# Revit family: 1
name_source: partatom
category: Pipe Accessories
units: mm (PartAtom-declared; Revit-internal decimal feet)

## family parameters
Always vertical = No
Cut with Voids When Loaded = No
Part Type = Valve - Breaks Into
Round Connector Dimension = Use Diameter
Shared = No
Work Plane-Based = No

## types (40) — shared parameters
1 = 1 mm  [stored 0.00328084 ft]
10 = 10 mm  [stored 0.0328084 ft]
20 = 25 mm  [stored 0.082021 ft]
5 = 5 mm  [stored 0.0164042 ft]
50 = 80 mm
54-0700-33-0101100 = DN700_ PN10_ CTC
54-0700-33-0102100 = DN700_ PN10_ CTC
54-0700-33-1101100 = DN700_ PN16_ CTC
54-0700-33-1102100 = DN700_ PN16_ CTC
54-0700-33-1103100 = DN700_ PN16_ CTC
54-0700-34-0101100 = DN700_ PN10_ CTO
54-0700-34-0102100 = DN700_ PN10_ CTO
54-0700-34-1101100 = DN700_ PN16_ CTO
54-0700-34-1102100 = DN700_ PN16_ CTO
54-0700-34-1103100 = DN700_ PN16_ CTO
54-0800-33-0101100 = DN800_ PN10_ CTC
54-0800-33-0102100 = DN800_ PN10_ CTC
54-0800-33-0103100 = DN800_ PN10_ CTC
54-0800-33-1101100 = DN800_ PN16_ CTC
54-0800-33-1102100 = DN800_ PN16_ CTC
54-0800-33-1103100 = DN800_ PN16_ CTC
54-0800-33-1104100 = DN800_ PN16_ CTC
54-0800-34-0101100 = DN800_ PN10_ CTO
54-0800-34-0102100 = DN800_ PN10_ CTO
54-0800-34-1101100 = DN800_ PN16_ CTO
54-0800-34-1102100 = DN800_ PN16_ CTO
54-0900-33-0102100 = DN900_ PN10_ CTC
54-0900-33-1101100 = DN900_ PN16_ CTC
54-0900-33-1102100 = DN900_ PN16_ CTC
54-0900-33-1103100 = DN900_ PN16_ CTC
54-0900-33-1104100 = DN900_ PN16_ CTC
54-0900-34-0102100 = DN900_ PN10_ CTO
54-0900-34-0104100 = DN900_ PN10_ CTO
54-0900-34-1101100 = DN900_ PN16_ CTO
54-0900-34-1102100 = DN900_ PN16_ CTO
54-0900-34-1103100 = DN900_ PN16_ CTO
54-1000-33-0102100 = DN1000_ PN10_ CTC
54-1000-33-0103100 = DN1000_ PN10_ CTC
54-1000-33-0104100 = DN1000_ PN10_ CTC
54-1000-33-1102100 = DN1000_ PN16_ CTC
54-1000-33-1103100 = DN1000_ PN16_ CTC
54-1000-33-1104100 = DN1000_ PN16_ CTC
54-1000-34-0102100 = DN1000_ PN10_ CTO
54-1000-34-1102100 = DN1000_ PN16_ CTO
54-1000-34-1103100 = DN1000_ PN16_ CTO
BP_centre = 13 mm  [stored 0.0426509 ft]
Bypass_DN = 100 mm
Bypass_FL_OD = 140 mm
Bypass_L = 70 mm
Bypass_R = 26 mm
Bypass_R1 = 52 mm
Bypass_Vale_D1 = 112 mm
Bypass_Vale_D2 = 98 mm
Bypass_Vale_D3 = 112 mm
Bypass_Vale_D6 = 168 mm
Bypass_W = 65 mm
Description_ = AVK GATE VALVE, FLANGED, METAL SEATED, PN10/16
H = 782 mm
Raised_dis = 5 mm  [stored 0.0164042 ft]
Search_table = 54-3334-001 DN700-1000
Stem_H1 = 150 mm
Stem_H2 = 127.5 mm
Stem_H3 = 202.5 mm
URL product pages = https://www.avkvalves.com
zero-valued in all types: Bonnet_dim22, Default Elevation

## per-type parameters (varying)
- 54-0700-33-0101100: ACtuator_T=23.4 mm  [stored 0.0767717 ft]; ADN=700 mm; Actuator_FLR=87.5 mm; Actuator_dim1=52.5 mm; Actuator_dim2=31.5 mm  [stored 0.103346 ft]; Actuator_dim3=57.75 mm; Body_H=748.5 mm; Body_L=792.3 mm; Body_T=292.5 mm; Body_W=267.2 mm; Body_rib_T=13 mm  [stored 0.0426509 ft]; Bonnet_FL_L=834 mm; Bonnet_FL_T=61.75 mm; Bonnet_FL_W=334 mm; Bonnet_dim1=158.46 mm; Bonnet_dim2=93.52 mm; Bonnet_dim3=1287.42 mm; Bonnet_fillet=29.69 mm; Bore=350 mm; Bypass_D7=416.85 mm; Bypass_Location=172 mm; Bypass_Vale_D4=60.12 mm; Bypass_Vale_D5=84.17 mm; Bypass_Vale_T=48.1 mm; Bypass_sweep=416.85 mm; Cut_dis=30.88 mm; DN=700 mm; F=35 mm  [stored 0.114829 ft]; F1=15.75 mm  [stored 0.0516732 ft]; F2=116 mm; FL_T=32.5 mm  [stored 0.106627 ft]; Fillet=89.07 mm; H1=1497 mm; H2=450 mm; L=610 mm; OD=895 mm; OD1=900 mm; PN=10 mm  [stored 0.0328084 ft]; Raised_dia=794 mm; Rib_Actual=679.5 mm; Rib_H=598.8 mm; Rib_H1=300 mm; Rib_H2=450 mm; Rib_H3=550 mm; Rib_H4=650 mm; Rib_L=375.3 mm; Rib_W=150.3 mm; Stem_D1=17.5 mm  [stored 0.0574147 ft]; Stem_D2=26.25 mm  [stored 0.086122 ft]; Stem_dim=43.75 mm; W=1359 mm; W-W1=525 mm; W1=834 mm; W_half=525 mm; bottom_rib=447.5 mm; stem_dim=38.67 mm; stem_dim1=56.88 mm; sweep=4 mm  [stored 0.0131234 ft]; sweep_start=397 mm; wedge_dim1=293.92 mm
- 54-0700-33-0102100: ACtuator_T=23.4 mm  [stored 0.0767717 ft]; ADN=700 mm; Actuator_FLR=105 mm; Actuator_dim1=63 mm; Actuator_dim2=37.8 mm; Actuator_dim3=69.3 mm; Body_H=748.5 mm; Body_L=792.3 mm; Body_T=292.5 mm; Body_W=267.2 mm; Body_rib_T=13 mm  [stored 0.0426509 ft]; Bonnet_FL_L=834 mm; Bonnet_FL_T=61.75 mm; Bonnet_FL_W=334 mm; Bonnet_dim1=158.46 mm; Bonnet_dim2=93.52 mm; Bonnet_dim3=1287.42 mm; Bonnet_fillet=29.69 mm; Bore=350.05 mm; Bypass_D7=416.85 mm; Bypass_Location=172 mm; Bypass_Vale_D4=60.12 mm; Bypass_Vale_D5=84.17 mm; Bypass_Vale_T=48.1 mm; Bypass_sweep=416.85 mm; Cut_dis=30.88 mm; DN=700.1 mm; F=42 mm; F1=18.9 mm  [stored 0.0620079 ft]; F2=129 mm; FL_T=32.5 mm  [stored 0.106627 ft]; Fillet=89.07 mm; H1=1497 mm; H2=450 mm; L=610 mm; OD=895 mm; OD1=900 mm; PN=10 mm  [stored 0.0328084 ft]; Raised_dia=794 mm; Rib_Actual=679.5 mm; Rib_H=598.8 mm; Rib_H1=300 mm; Rib_H2=450 mm; Rib_H3=550 mm; Rib_H4=650 mm; Rib_L=375.3 mm; Rib_W=150.3 mm; Stem_D1=21 mm  [stored 0.0688976 ft]; Stem_D2=31.5 mm  [stored 0.103346 ft]; Stem_dim=52.5 mm; W=1359 mm; W-W1=525 mm; W1=834 mm; W_half=525 mm; bottom_rib=447.5 mm; stem_dim=43 mm; stem_dim1=68.25 mm; sweep=4 mm  [stored 0.0131234 ft]; sweep_start=397 mm; wedge_dim1=293.92 mm
- 54-0700-33-1101100: ACtuator_T=28.44 mm; ADN=700 mm; Actuator_FLR=87.5 mm; Actuator_dim1=52.5 mm; Actuator_dim2=31.5 mm  [stored 0.103346 ft]; Actuator_dim3=57.75 mm; Body_H=748.5 mm; Body_L=792.3 mm; Body_T=292.5 mm; Body_W=267.2 mm; Body_rib_T=15.8 mm  [stored 0.0518373 ft]; Bonnet_FL_L=834 mm; Bonnet_FL_T=75.05 mm; Bonnet_FL_W=334 mm; Bonnet_dim1=158.46 mm; Bonnet_dim2=93.52 mm; Bonnet_dim3=1287.42 mm; Bonnet_fillet=29.69 mm; Bore=350.06 mm; Bypass_D7=378 mm; Bypass_Location=172 mm; Bypass_Vale_D4=60.12 mm; Bypass_Vale_D5=84.17 mm; Bypass_Vale_T=48.1 mm; Bypass_sweep=378 mm; Cut_dis=37.53 mm; DN=700.11 mm; F=35 mm  [stored 0.114829 ft]; F1=15.75 mm  [stored 0.0516732 ft]; F2=116 mm; FL_T=39.5 mm; Fillet=89.07 mm; H1=1497 mm; H2=450 mm; L=610 mm; OD=880 mm; OD1=900 mm; PN=16 mm  [stored 0.0524934 ft]; Raised_dia=720 mm; Rib_Actual=679.5 mm; Rib_H=598.8 mm; Rib_H1=300 mm; Rib_H2=450 mm; Rib_H3=550 mm; Rib_H4=650 mm; Rib_L=375.3 mm; Rib_W=150.3 mm; Stem_D1=17.5 mm  [stored 0.0574147 ft]; Stem_D2=26.25 mm  [stored 0.086122 ft]; Stem_dim=43.75 mm; W=1359 mm; W-W1=525 mm; W1=834 mm; W_half=525 mm; bottom_rib=440 mm; stem_dim=38.67 mm; stem_dim1=56.88 mm; sweep=4 mm  [stored 0.0131234 ft]; sweep_start=360 mm; wedge_dim1=293.92 mm
- 54-0700-33-1102100: ACtuator_T=28.44 mm; ADN=700 mm; Actuator_FLR=105 mm; Actuator_dim1=63 mm; Actuator_dim2=37.8 mm; Actuator_dim3=69.3 mm; Body_H=748.5 mm; Body_L=792.3 mm; Body_T=292.5 mm; Body_W=267.2 mm; Body_rib_T=15.8 mm  [stored 0.0518373 ft]; Bonnet_FL_L=834 mm; Bonnet_FL_T=75.05 mm; Bonnet_FL_W=334 mm; Bonnet_dim1=158.46 mm; Bonnet_dim2=93.52 mm; Bonnet_dim3=1287.42 mm; Bonnet_fillet=29.69 mm; Bore=350.06 mm; Bypass_D7=378 mm; Bypass_Location=172 mm; Bypass_Vale_D4=60.12 mm; Bypass_Vale_D5=84.17 mm; Bypass_Vale_T=48.1 mm; Bypass_sweep=378 mm; Cut_dis=37.53 mm; DN=700.12 mm; F=42 mm; F1=18.9 mm  [stored 0.0620079 ft]; F2=129 mm; FL_T=39.5 mm; Fillet=89.07 mm; H1=1497 mm; H2=450 mm; L=610 mm; OD=880 mm; OD1=900 mm; PN=16 mm  [stored 0.0524934 ft]; Raised_dia=720 mm; Rib_Actual=679.5 mm; Rib_H=598.8 mm; Rib_H1=300 mm; Rib_H2=450 mm; Rib_H3=550 mm; Rib_H4=650 mm; Rib_L=375.3 mm; Rib_W=150.3 mm; Stem_D1=21 mm  [stored 0.0688976 ft]; Stem_D2=31.5 mm  [stored 0.103346 ft]; Stem_dim=52.5 mm; W=1359 mm; W-W1=525 mm; W1=834 mm; W_half=525 mm; bottom_rib=440 mm; stem_dim=43 mm; stem_dim1=68.25 mm; sweep=4 mm  [stored 0.0131234 ft]; sweep_start=360 mm; wedge_dim1=293.92 mm
- 54-0700-33-1103100: ACtuator_T=28.44 mm; ADN=700 mm; Actuator_FLR=150 mm; Actuator_dim1=90 mm; Actuator_dim2=54 mm; Actuator_dim3=99 mm; Body_H=748.5 mm; Body_L=997.5 mm; Body_T=342.5 mm; Body_W=291.2 mm; Body_rib_T=15.8 mm  [stored 0.0518373 ft]; Bonnet_FL_L=1050 mm; Bonnet_FL_T=75.05 mm; Bonnet_FL_W=364 mm; Bonnet_dim1=199.5 mm; Bonnet_dim2=101.92 mm; Bonnet_dim3=1287.42 mm; Bonnet_fillet=32.36 mm; Bore=350.07 mm; Bypass_D7=416.85 mm; Bypass_Location=172 mm; Bypass_Vale_D4=65.52 mm; Bypass_Vale_D5=91.73 mm; Bypass_Vale_T=52.42 mm; Bypass_sweep=416.85 mm; Cut_dis=37.53 mm; DN=700.13 mm; F=60 mm; F1=27 mm  [stored 0.0885827 ft]; F2=169 mm; FL_T=39.5 mm; Fillet=97.07 mm; H1=1497 mm; H2=450 mm; L=610 mm; OD=900 mm; OD1=900 mm; PN=16 mm  [stored 0.0524934 ft]; Raised_dia=794 mm; Rib_Actual=679.5 mm; Rib_H=598.8 mm; Rib_H1=300 mm; Rib_H2=450 mm; Rib_H3=550 mm; Rib_H4=650 mm; Rib_L=472.5 mm; Rib_W=163.8 mm; Stem_D1=30 mm  [stored 0.0984252 ft]; Stem_D2=45 mm; Stem_dim=75 mm; W=1359 mm; W-W1=525 mm; W1=834 mm; W_half=525 mm; bottom_rib=450 mm; stem_dim=56.33 mm; stem_dim1=97.5 mm; sweep=5 mm  [stored 0.0164042 ft]; sweep_start=397 mm; wedge_dim1=320.32 mm
- 54-0700-34-0101100: ACtuator_T=23.4 mm  [stored 0.0767717 ft]; ADN=700 mm; Actuator_FLR=87.5 mm; Actuator_dim1=52.5 mm; Actuator_dim2=31.5 mm  [stored 0.103346 ft]; Actuator_dim3=57.75 mm; Body_H=748.5 mm; Body_L=997.5 mm; Body_T=342.5 mm; Body_W=291.2 mm; Body_rib_T=13 mm  [stored 0.0426509 ft]; Bonnet_FL_L=1050 mm; Bonnet_FL_T=61.75 mm; Bonnet_FL_W=364 mm; Bonnet_dim1=199.5 mm; Bonnet_dim2=101.92 mm; Bonnet_dim3=1287.42 mm; Bonnet_fillet=32.36 mm; Bore=350.07 mm; Bypass_D7=416.85 mm; Bypass_Location=172 mm; Bypass_Vale_D4=65.52 mm; Bypass_Vale_D5=91.73 mm; Bypass_Vale_T=52.42 mm; Bypass_sweep=416.85 mm; Cut_dis=30.88 mm; DN=700.14 mm; F=35 mm  [stored 0.114829 ft]; F1=15.75 mm  [stored 0.0516732 ft]; F2=116 mm; FL_T=32.5 mm  [stored 0.106627 ft]; Fillet=97.07 mm; H1=1497 mm; H2=450 mm; L=610 mm; OD=895 mm; OD1=900 mm; PN=10 mm  [stored 0.0328084 ft]; Raised_dia=794 mm; Rib_Actual=679.5 mm; Rib_H=598.8 mm; Rib_H1=300 mm; Rib_H2=450 mm; Rib_H3=550 mm; Rib_H4=650 mm; Rib_L=472.5 mm; Rib_W=163.8 mm; Stem_D1=17.5 mm  [stored 0.0574147 ft]; Stem_D2=26.25 mm  [stored 0.086122 ft]; Stem_dim=43.75 mm; W=1359 mm; W-W1=525 mm; W1=834 mm; W_half=525 mm; bottom_rib=447.5 mm; stem_dim=38.67 mm; stem_dim1=56.88 mm; sweep=5 mm  [stored 0.0164042 ft]; sweep_start=397 mm; wedge_dim1=320.32 mm
- 54-0700-34-0102100: ACtuator_T=23.4 mm  [stored 0.0767717 ft]; ADN=700 mm; Actuator_FLR=105 mm; Actuator_dim1=63 mm; Actuator_dim2=37.8 mm; Actuator_dim3=69.3 mm; Body_H=748.5 mm; Body_L=997.5 mm; Body_T=342.5 mm; Body_W=291.2 mm; Body_rib_T=13 mm  [stored 0.0426509 ft]; Bonnet_FL_L=1050 mm; Bonnet_FL_T=61.75 mm; Bonnet_FL_W=364 mm; Bonnet_dim1=199.5 mm; Bonnet_dim2=101.92 mm; Bonnet_dim3=1287.42 mm; Bonnet_fillet=32.36 mm; Bore=350.08 mm; Bypass_D7=416.85 mm; Bypass_Location=172 mm; Bypass_Vale_D4=65.52 mm; Bypass_Vale_D5=91.73 mm; Bypass_Vale_T=52.42 mm; Bypass_sweep=416.85 mm; Cut_dis=30.88 mm; DN=700.15 mm; F=42 mm; F1=18.9 mm  [stored 0.0620079 ft]; F2=129 mm; FL_T=32.5 mm  [stored 0.106627 ft]; Fillet=97.07 mm; H1=1497 mm; H2=450 mm; L=610 mm; OD=895 mm; OD1=900 mm; PN=10 mm  [stored 0.0328084 ft]; Raised_dia=794 mm; Rib_Actual=679.5 mm; Rib_H=598.8 mm; Rib_H1=300 mm; Rib_H2=450 mm; Rib_H3=550 mm; Rib_H4=650 mm; Rib_L=472.5 mm; Rib_W=163.8 mm; Stem_D1=21 mm  [stored 0.0688976 ft]; Stem_D2=31.5 mm  [stored 0.103346 ft]; Stem_dim=52.5 mm; W=1359 mm; W-W1=525 mm; W1=834 mm; W_half=525 mm; bottom_rib=447.5 mm; stem_dim=43 mm; stem_dim1=68.25 mm; sweep=5 mm  [stored 0.0164042 ft]; sweep_start=397 mm; wedge_dim1=320.32 mm
- 54-0700-34-1101100: ACtuator_T=28.44 mm; ADN=700 mm; Actuator_FLR=87.5 mm; Actuator_dim1=52.5 mm; Actuator_dim2=31.5 mm  [stored 0.103346 ft]; Actuator_dim3=57.75 mm; Body_H=748.5 mm; Body_L=997.5 mm; Body_T=342.5 mm; Body_W=291.2 mm; Body_rib_T=15.8 mm  [stored 0.0518373 ft]; Bonnet_FL_L=1050 mm; Bonnet_FL_T=75.05 mm; Bonnet_FL_W=364 mm; Bonnet_dim1=199.5 mm; Bonnet_dim2=101.92 mm; Bonnet_dim3=1287.42 mm; Bonnet_fillet=32.36 mm; Bore=350.08 mm; Bypass_D7=416.85 mm; Bypass_Location=172 mm; Bypass_Vale_D4=65.52 mm; Bypass_Vale_D5=91.73 mm; Bypass_Vale_T=52.42 mm; Bypass_sweep=416.85 mm; Cut_dis=37.53 mm; DN=700.16 mm; F=35 mm  [stored 0.114829 ft]; F1=15.75 mm  [stored 0.0516732 ft]; F2=116 mm; FL_T=39.5 mm; Fillet=97.07 mm; H1=1497 mm; H2=450 mm; L=610 mm; OD=900 mm; OD1=900 mm; PN=16 mm  [stored 0.0524934 ft]; Raised_dia=794 mm; Rib_Actual=679.5 mm; Rib_H=598.8 mm; Rib_H1=300 mm; Rib_H2=450 mm; Rib_H3=550 mm; Rib_H4=650 mm; Rib_L=472.5 mm; Rib_W=163.8 mm; Stem_D1=17.5 mm  [stored 0.0574147 ft]; Stem_D2=26.25 mm  [stored 0.086122 ft]; Stem_dim=43.75 mm; W=1359 mm; W-W1=525 mm; W1=834 mm; W_half=525 mm; bottom_rib=450 mm; stem_dim=38.67 mm; stem_dim1=56.88 mm; sweep=5 mm  [stored 0.0164042 ft]; sweep_start=397 mm; wedge_dim1=320.32 mm
- 54-0700-34-1102100: ACtuator_T=28.44 mm; ADN=700 mm; Actuator_FLR=105 mm; Actuator_dim1=63 mm; Actuator_dim2=37.8 mm; Actuator_dim3=69.3 mm; Body_H=748.5 mm; Body_L=997.5 mm; Body_T=342.5 mm; Body_W=291.2 mm; Body_rib_T=15.8 mm  [stored 0.0518373 ft]; Bonnet_FL_L=1050 mm; Bonnet_FL_T=75.05 mm; Bonnet_FL_W=364 mm; Bonnet_dim1=199.5 mm; Bonnet_dim2=101.92 mm; Bonnet_dim3=1287.42 mm; Bonnet_fillet=32.36 mm; Bore=350.09 mm; Bypass_D7=416.85 mm; Bypass_Location=172 mm; Bypass_Vale_D4=65.52 mm; Bypass_Vale_D5=91.73 mm; Bypass_Vale_T=52.42 mm; Bypass_sweep=416.85 mm; Cut_dis=37.53 mm; DN=700.17 mm; F=42 mm; F1=18.9 mm  [stored 0.0620079 ft]; F2=129 mm; FL_T=39.5 mm; Fillet=97.07 mm; H1=1497 mm; H2=450 mm; L=610 mm; OD=900 mm; OD1=900 mm; PN=16 mm  [stored 0.0524934 ft]; Raised_dia=794 mm; Rib_Actual=679.5 mm; Rib_H=598.8 mm; Rib_H1=300 mm; Rib_H2=450 mm; Rib_H3=550 mm; Rib_H4=650 mm; Rib_L=472.5 mm; Rib_W=163.8 mm; Stem_D1=21 mm  [stored 0.0688976 ft]; Stem_D2=31.5 mm  [stored 0.103346 ft]; Stem_dim=52.5 mm; W=1359 mm; W-W1=525 mm; W1=834 mm; W_half=525 mm; bottom_rib=450 mm; stem_dim=43 mm; stem_dim1=68.25 mm; sweep=5 mm  [stored 0.0164042 ft]; sweep_start=397 mm; wedge_dim1=320.32 mm
- 54-0700-34-1103100: ACtuator_T=28.44 mm; ADN=700 mm; Actuator_FLR=150 mm; Actuator_dim1=90 mm; Actuator_dim2=54 mm; Actuator_dim3=99 mm; Body_H=748.5 mm; Body_L=997.5 mm; Body_T=342.5 mm; Body_W=291.2 mm; Body_rib_T=15.8 mm  [stored 0.0518373 ft]; Bonnet_FL_L=1050 mm; Bonnet_FL_T=75.05 mm; Bonnet_FL_W=364 mm; Bonnet_dim1=199.5 mm; Bonnet_dim2=101.92 mm; Bonnet_dim3=1287.42 mm; Bonnet_fillet=32.36 mm; Bore=350.09 mm; Bypass_D7=416.85 mm; Bypass_Location=172 mm; Bypass_Vale_D4=65.52 mm; Bypass_Vale_D5=91.73 mm; Bypass_Vale_T=52.42 mm; Bypass_sweep=416.85 mm; Cut_dis=37.53 mm; DN=700.18 mm; F=60 mm; F1=27 mm  [stored 0.0885827 ft]; F2=169 mm; FL_T=39.5 mm; Fillet=97.07 mm; H1=1497 mm; H2=450 mm; L=610 mm; OD=900 mm; OD1=900 mm; PN=16 mm  [stored 0.0524934 ft]; Raised_dia=794 mm; Rib_Actual=679.5 mm; Rib_H=598.8 mm; Rib_H1=300 mm; Rib_H2=450 mm; Rib_H3=550 mm; Rib_H4=650 mm; Rib_L=472.5 mm; Rib_W=163.8 mm; Stem_D1=30 mm  [stored 0.0984252 ft]; Stem_D2=45 mm; Stem_dim=75 mm; W=1359 mm; W-W1=525 mm; W1=834 mm; W_half=525 mm; bottom_rib=450 mm; stem_dim=56.33 mm; stem_dim1=97.5 mm; sweep=5 mm  [stored 0.0164042 ft]; sweep_start=397 mm; wedge_dim1=320.32 mm
- 54-0800-33-0101100: ACtuator_T=25.2 mm  [stored 0.0826772 ft]; ADN=800 mm; Actuator_FLR=87.5 mm; Actuator_dim1=52.5 mm; Actuator_dim2=31.5 mm  [stored 0.103346 ft]; Actuator_dim3=57.75 mm; Body_H=844.5 mm; Body_L=997.5 mm; Body_T=342.5 mm; Body_W=291.2 mm; Body_rib_T=14 mm  [stored 0.0459318 ft]; Bonnet_FL_L=1050 mm; Bonnet_FL_T=66.5 mm; Bonnet_FL_W=364 mm; Bonnet_dim1=199.5 mm; Bonnet_dim2=101.92 mm; Bonnet_dim3=1452.54 mm; Bonnet_fillet=32.36 mm; Bore=400 mm; Bypass_D7=473.03 mm; Bypass_Location=172 mm; Bypass_Vale_D4=65.52 mm; Bypass_Vale_D5=91.73 mm; Bypass_Vale_T=52.42 mm; Bypass_sweep=473.03 mm; Cut_dis=33.25 mm  [stored 0.109088 ft]; DN=800 mm; F=35 mm  [stored 0.114829 ft]; F1=15.75 mm  [stored 0.0516732 ft]; F2=116 mm; FL_T=35 mm  [stored 0.114829 ft]; Fillet=97.07 mm; H1=1689 mm; H2=535 mm; L=660 mm; OD=1015 mm; OD1=1070 mm; PN=10 mm  [stored 0.0328084 ft]; Raised_dia=901 mm; Rib_Actual=744 mm; Rib_H=675.6 mm; Rib_H1=190 mm; Rib_H2=550 mm; Rib_H3=650 mm; Rib_H4=750 mm; Rib_L=472.5 mm; Rib_W=163.8 mm; Stem_D1=17.5 mm  [stored 0.0574147 ft]; Stem_D2=26.25 mm  [stored 0.086122 ft]; Stem_dim=43.75 mm; W=1488 mm; W-W1=580 mm; W1=908 mm; W_half=580 mm; bottom_rib=507.5 mm; stem_dim=38.67 mm; stem_dim1=56.88 mm; sweep=5 mm  [stored 0.0164042 ft]; sweep_start=450.5 mm; wedge_dim1=320.32 mm
- 54-0800-33-0102100: ACtuator_T=25.2 mm  [stored 0.0826772 ft]; ADN=800 mm; Actuator_FLR=105 mm; Actuator_dim1=63 mm; Actuator_dim2=37.8 mm; Actuator_dim3=69.3 mm; Body_H=844.5 mm; Body_L=997.5 mm; Body_T=342.5 mm; Body_W=291.2 mm; Body_rib_T=14 mm  [stored 0.0459318 ft]; Bonnet_FL_L=1050 mm; Bonnet_FL_T=66.5 mm; Bonnet_FL_W=364 mm; Bonnet_dim1=199.5 mm; Bonnet_dim2=101.92 mm; Bonnet_dim3=1452.54 mm; Bonnet_fillet=32.36 mm; Bore=400.05 mm; Bypass_D7=473.03 mm; Bypass_Location=172 mm; Bypass_Vale_D4=65.52 mm; Bypass_Vale_D5=91.73 mm; Bypass_Vale_T=52.42 mm; Bypass_sweep=473.03 mm; Cut_dis=33.25 mm  [stored 0.109088 ft]; DN=800.1 mm; F=42 mm; F1=18.9 mm  [stored 0.0620079 ft]; F2=129 mm; FL_T=35 mm  [stored 0.114829 ft]; Fillet=97.07 mm; H1=1689 mm; H2=535 mm; L=660 mm; OD=1015 mm; OD1=1070 mm; PN=10 mm  [stored 0.0328084 ft]; Raised_dia=901 mm; Rib_Actual=744 mm; Rib_H=675.6 mm; Rib_H1=190 mm; Rib_H2=550 mm; Rib_H3=650 mm; Rib_H4=750 mm; Rib_L=472.5 mm; Rib_W=163.8 mm; Stem_D1=21 mm  [stored 0.0688976 ft]; Stem_D2=31.5 mm  [stored 0.103346 ft]; Stem_dim=52.5 mm; W=1488 mm; W-W1=580 mm; W1=908 mm; W_half=580 mm; bottom_rib=507.5 mm; stem_dim=43 mm; stem_dim1=68.25 mm; sweep=5 mm  [stored 0.0164042 ft]; sweep_start=450.5 mm; wedge_dim1=320.32 mm
- 54-0800-33-0103100: ACtuator_T=25.2 mm  [stored 0.0826772 ft]; ADN=800 mm; Actuator_FLR=150 mm; Actuator_dim1=90 mm; Actuator_dim2=54 mm; Actuator_dim3=99 mm; Body_H=844.5 mm; Body_L=997.5 mm; Body_T=342.5 mm; Body_W=291.2 mm; Body_rib_T=14 mm  [stored 0.0459318 ft]; Bonnet_FL_L=1050 mm; Bonnet_FL_T=66.5 mm; Bonnet_FL_W=364 mm; Bonnet_dim1=199.5 mm; Bonnet_dim2=101.92 mm; Bonnet_dim3=1452.54 mm; Bonnet_fillet=32.36 mm; Bore=400.06 mm; Bypass_D7=473.03 mm; Bypass_Location=172 mm; Bypass_Vale_D4=65.52 mm; Bypass_Vale_D5=91.73 mm; Bypass_Vale_T=52.42 mm; Bypass_sweep=473.03 mm; Cut_dis=33.25 mm  [stored 0.109088 ft]; DN=800.11 mm; F=60 mm; F1=27 mm  [stored 0.0885827 ft]; F2=169 mm; FL_T=35 mm  [stored 0.114829 ft]; Fillet=97.07 mm; H1=1689 mm; H2=535 mm; L=660 mm; OD=1015 mm; OD1=1070 mm; PN=10 mm  [stored 0.0328084 ft]; Raised_dia=901 mm; Rib_Actual=744 mm; Rib_H=675.6 mm; Rib_H1=190 mm; Rib_H2=550 mm; Rib_H3=650 mm; Rib_H4=750 mm; Rib_L=472.5 mm; Rib_W=163.8 mm; Stem_D1=30 mm  [stored 0.0984252 ft]; Stem_D2=45 mm; Stem_dim=75 mm; W=1488 mm; W-W1=580 mm; W1=908 mm; W_half=580 mm; bottom_rib=507.5 mm; stem_dim=56.33 mm; stem_dim1=97.5 mm; sweep=5 mm  [stored 0.0164042 ft]; sweep_start=450.5 mm; wedge_dim1=320.32 mm
- 54-0800-33-1101100: ACtuator_T=30.96 mm  [stored 0.101575 ft]; ADN=800 mm; Actuator_FLR=87.5 mm; Actuator_dim1=52.5 mm; Actuator_dim2=31.5 mm  [stored 0.103346 ft]; Actuator_dim3=57.75 mm; Body_H=844.5 mm; Body_L=997.5 mm; Body_T=342.5 mm; Body_W=291.2 mm; Body_rib_T=17.2 mm; Bonnet_FL_L=1050 mm; Bonnet_FL_T=81.7 mm; Bonnet_FL_W=364 mm; Bonnet_dim1=199.5 mm; Bonnet_dim2=101.92 mm; Bonnet_dim3=1452.54 mm; Bonnet_fillet=32.36 mm; Bore=400.06 mm; Bypass_D7=473.03 mm; Bypass_Location=172 mm; Bypass_Vale_D4=65.52 mm; Bypass_Vale_D5=91.73 mm; Bypass_Vale_T=52.42 mm; Bypass_sweep=473.03 mm; Cut_dis=40.85 mm; DN=800.12 mm; F=35 mm  [stored 0.114829 ft]; F1=15.75 mm  [stored 0.0516732 ft]; F2=116 mm; FL_T=43 mm; Fillet=97.07 mm; H1=1689 mm; H2=535 mm; L=660 mm; OD=1070 mm; OD1=1070 mm; PN=16 mm  [stored 0.0524934 ft]; Raised_dia=901 mm; Rib_Actual=744 mm; Rib_H=675.6 mm; Rib_H1=190 mm; Rib_H2=550 mm; Rib_H3=650 mm; Rib_H4=750 mm; Rib_L=472.5 mm; Rib_W=163.8 mm; Stem_D1=17.5 mm  [stored 0.0574147 ft]; Stem_D2=26.25 mm  [stored 0.086122 ft]; Stem_dim=43.75 mm; W=1488 mm; W-W1=580 mm; W1=908 mm; W_half=580 mm; bottom_rib=535 mm; stem_dim=38.67 mm; stem_dim1=56.88 mm; sweep=5 mm  [stored 0.0164042 ft]; sweep_start=450.5 mm; wedge_dim1=320.32 mm
- 54-0800-33-1102100: ACtuator_T=30.96 mm  [stored 0.101575 ft]; ADN=800 mm; Actuator_FLR=105 mm; Actuator_dim1=63 mm; Actuator_dim2=37.8 mm; Actuator_dim3=69.3 mm; Body_H=844.5 mm; Body_L=1102 mm; Body_T=392.5 mm; Body_W=312.8 mm; Body_rib_T=17.2 mm; Bonnet_FL_L=1160 mm; Bonnet_FL_T=81.7 mm; Bonnet_FL_W=391 mm; Bonnet_dim1=220.4 mm; Bonnet_dim2=109.48 mm; Bonnet_dim3=1452.54 mm; Bonnet_fillet=34.76 mm; Bore=400.07 mm; Bypass_D7=473.03 mm; Bypass_Location=172 mm; Bypass_Vale_D4=70.38 mm; Bypass_Vale_D5=98.53 mm; Bypass_Vale_T=56.3 mm; Bypass_sweep=473.03 mm; Cut_dis=40.85 mm; DN=800.13 mm; F=42 mm; F1=18.9 mm  [stored 0.0620079 ft]; F2=129 mm; FL_T=43 mm; Fillet=104.27 mm; H1=1689 mm; H2=535 mm; L=660 mm; OD=1070 mm; OD1=1070 mm; PN=16 mm  [stored 0.0524934 ft]; Raised_dia=901 mm; Rib_Actual=744 mm; Rib_H=675.6 mm; Rib_H1=190 mm; Rib_H2=550 mm; Rib_H3=650 mm; Rib_H4=750 mm; Rib_L=522 mm; Rib_W=175.95 mm; Stem_D1=21 mm  [stored 0.0688976 ft]; Stem_D2=31.5 mm  [stored 0.103346 ft]; Stem_dim=52.5 mm; W=1488 mm; W-W1=580 mm; W1=908 mm; W_half=580 mm; bottom_rib=535 mm; stem_dim=43 mm; stem_dim1=68.25 mm; sweep=5 mm  [stored 0.0164042 ft]; sweep_start=450.5 mm; wedge_dim1=344.08 mm
- 54-0800-33-1103100: ACtuator_T=30.96 mm  [stored 0.101575 ft]; ADN=800 mm; Actuator_FLR=150 mm; Actuator_dim1=90 mm; Actuator_dim2=54 mm; Actuator_dim3=99 mm; Body_H=844.5 mm; Body_L=1102 mm; Body_T=392.5 mm; Body_W=312.8 mm; Body_rib_T=17.2 mm; Bonnet_FL_L=1160 mm; Bonnet_FL_T=81.7 mm; Bonnet_FL_W=391 mm; Bonnet_dim1=220.4 mm; Bonnet_dim2=109.48 mm; Bonnet_dim3=1452.54 mm; Bonnet_fillet=34.76 mm; Bore=400.07 mm; Bypass_D7=473.03 mm; Bypass_Location=172 mm; Bypass_Vale_D4=70.38 mm; Bypass_Vale_D5=98.53 mm; Bypass_Vale_T=56.3 mm; Bypass_sweep=473.03 mm; Cut_dis=40.85 mm; DN=800.14 mm; F=60 mm; F1=27 mm  [stored 0.0885827 ft]; F2=169 mm; FL_T=43 mm; Fillet=104.27 mm; H1=1689 mm; H2=535 mm; L=660 mm; OD=1070 mm; OD1=1070 mm; PN=16 mm  [stored 0.0524934 ft]; Raised_dia=901 mm; Rib_Actual=744 mm; Rib_H=675.6 mm; Rib_H1=190 mm; Rib_H2=550 mm; Rib_H3=650 mm; Rib_H4=750 mm; Rib_L=522 mm; Rib_W=175.95 mm; Stem_D1=30 mm  [stored 0.0984252 ft]; Stem_D2=45 mm; Stem_dim=75 mm; W=1488 mm; W-W1=580 mm; W1=908 mm; W_half=580 mm; bottom_rib=535 mm; stem_dim=56.33 mm; stem_dim1=97.5 mm; sweep=5 mm  [stored 0.0164042 ft]; sweep_start=450.5 mm; wedge_dim1=344.08 mm
- 54-0800-33-1104100: ACtuator_T=30.96 mm  [stored 0.101575 ft]; ADN=800 mm; Actuator_FLR=175 mm; Actuator_dim1=105 mm; Actuator_dim2=63 mm; Actuator_dim3=115.5 mm; Body_H=844.5 mm; Body_L=1102 mm; Body_T=392.5 mm; Body_W=312.8 mm; Body_rib_T=17.2 mm; Bonnet_FL_L=1160 mm; Bonnet_FL_T=81.7 mm; Bonnet_FL_W=391 mm; Bonnet_dim1=220.4 mm; Bonnet_dim2=109.48 mm; Bonnet_dim3=1452.54 mm; Bonnet_fillet=34.76 mm; Bore=400.08 mm; Bypass_D7=473.03 mm; Bypass_Location=172 mm; Bypass_Vale_D4=70.38 mm; Bypass_Vale_D5=98.53 mm; Bypass_Vale_T=56.3 mm; Bypass_sweep=473.03 mm; Cut_dis=40.85 mm; DN=800.15 mm; F=70 mm; F1=31.5 mm  [stored 0.103346 ft]; F2=199 mm; FL_T=43 mm; Fillet=104.27 mm; H1=1689 mm; H2=535 mm; L=660 mm; OD=1070 mm; OD1=1070 mm; PN=16 mm  [stored 0.0524934 ft]; Raised_dia=901 mm; Rib_Actual=744 mm; Rib_H=675.6 mm; Rib_H1=190 mm; Rib_H2=550 mm; Rib_H3=650 mm; Rib_H4=750 mm; Rib_L=522 mm; Rib_W=175.95 mm; Stem_D1=35 mm  [stored 0.114829 ft]; Stem_D2=52.5 mm; Stem_dim=87.5 mm; W=1488 mm; W-W1=580 mm; W1=908 mm; W_half=580 mm; bottom_rib=535 mm; stem_dim=66.33 mm; stem_dim1=113.75 mm; sweep=5 mm  [stored 0.0164042 ft]; sweep_start=450.5 mm; wedge_dim1=344.08 mm
- 54-0800-34-0101100: ACtuator_T=25.2 mm  [stored 0.0826772 ft]; ADN=800 mm; Actuator_FLR=87.5 mm; Actuator_dim1=52.5 mm; Actuator_dim2=31.5 mm  [stored 0.103346 ft]; Actuator_dim3=57.75 mm; Body_H=844.5 mm; Body_L=1102 mm; Body_T=392.5 mm; Body_W=312.8 mm; Body_rib_T=14 mm  [stored 0.0459318 ft]; Bonnet_FL_L=1160 mm; Bonnet_FL_T=66.5 mm; Bonnet_FL_W=391 mm; Bonnet_dim1=220.4 mm; Bonnet_dim2=109.48 mm; Bonnet_dim3=1452.54 mm; Bonnet_fillet=34.76 mm; Bore=400.08 mm; Bypass_D7=473.03 mm; Bypass_Location=172 mm; Bypass_Vale_D4=70.38 mm; Bypass_Vale_D5=98.53 mm; Bypass_Vale_T=56.3 mm; Bypass_sweep=473.03 mm; Cut_dis=33.25 mm  [stored 0.109088 ft]; DN=800.16 mm; F=35 mm  [stored 0.114829 ft]; F1=15.75 mm  [stored 0.0516732 ft]; F2=116 mm; FL_T=35 mm  [stored 0.114829 ft]; Fillet=104.27 mm; H1=1689 mm; H2=535 mm; L=660 mm; OD=1015 mm; OD1=1070 mm; PN=10 mm  [stored 0.0328084 ft]; Raised_dia=901 mm; Rib_Actual=744 mm; Rib_H=675.6 mm; Rib_H1=190 mm; Rib_H2=550 mm; Rib_H3=650 mm; Rib_H4=750 mm; Rib_L=522 mm; Rib_W=175.95 mm; Stem_D1=17.5 mm  [stored 0.0574147 ft]; Stem_D2=26.25 mm  [stored 0.086122 ft]; Stem_dim=43.75 mm; W=1488 mm; W-W1=580 mm; W1=908 mm; W_half=580 mm; bottom_rib=507.5 mm; stem_dim=38.67 mm; stem_dim1=56.88 mm; sweep=5 mm  [stored 0.0164042 ft]; sweep_start=450.5 mm; wedge_dim1=344.08 mm
- 54-0800-34-0102100: ACtuator_T=25.2 mm  [stored 0.0826772 ft]; ADN=800 mm; Actuator_FLR=105 mm; Actuator_dim1=63 mm; Actuator_dim2=37.8 mm; Actuator_dim3=69.3 mm; Body_H=844.5 mm; Body_L=1102 mm; Body_T=392.5 mm; Body_W=312.8 mm; Body_rib_T=14 mm  [stored 0.0459318 ft]; Bonnet_FL_L=1160 mm; Bonnet_FL_T=66.5 mm; Bonnet_FL_W=391 mm; Bonnet_dim1=220.4 mm; Bonnet_dim2=109.48 mm; Bonnet_dim3=1452.54 mm; Bonnet_fillet=34.76 mm; Bore=400.09 mm; Bypass_D7=473.03 mm; Bypass_Location=172 mm; Bypass_Vale_D4=70.38 mm; Bypass_Vale_D5=98.53 mm; Bypass_Vale_T=56.3 mm; Bypass_sweep=473.03 mm; Cut_dis=33.25 mm  [stored 0.109088 ft]; DN=800.17 mm; F=42 mm; F1=18.9 mm  [stored 0.0620079 ft]; F2=129 mm; FL_T=35 mm  [stored 0.114829 ft]; Fillet=104.27 mm; H1=1689 mm; H2=535 mm; L=660 mm; OD=1015 mm; OD1=1070 mm; PN=10 mm  [stored 0.0328084 ft]; Raised_dia=901 mm; Rib_Actual=744 mm; Rib_H=675.6 mm; Rib_H1=190 mm; Rib_H2=550 mm; Rib_H3=650 mm; Rib_H4=750 mm; Rib_L=522 mm; Rib_W=175.95 mm; Stem_D1=21 mm  [stored 0.0688976 ft]; Stem_D2=31.5 mm  [stored 0.103346 ft]; Stem_dim=52.5 mm; W=1488 mm; W-W1=580 mm; W1=908 mm; W_half=580 mm; bottom_rib=507.5 mm; stem_dim=43 mm; stem_dim1=68.25 mm; sweep=5 mm  [stored 0.0164042 ft]; sweep_start=450.5 mm; wedge_dim1=344.08 mm
- 54-0800-34-1101100: ACtuator_T=30.96 mm  [stored 0.101575 ft]; ADN=800 mm; Actuator_FLR=87.5 mm; Actuator_dim1=52.5 mm; Actuator_dim2=31.5 mm  [stored 0.103346 ft]; Actuator_dim3=57.75 mm; Body_H=844.5 mm; Body_L=1102 mm; Body_T=392.5 mm; Body_W=312.8 mm; Body_rib_T=17.2 mm; Bonnet_FL_L=1160 mm; Bonnet_FL_T=81.7 mm; Bonnet_FL_W=391 mm; Bonnet_dim1=220.4 mm; Bonnet_dim2=109.48 mm; Bonnet_dim3=1452.54 mm; Bonnet_fillet=34.76 mm; Bore=400.09 mm; Bypass_D7=473.03 mm; Bypass_Location=172 mm; Bypass_Vale_D4=70.38 mm; Bypass_Vale_D5=98.53 mm; Bypass_Vale_T=56.3 mm; Bypass_sweep=473.03 mm; Cut_dis=40.85 mm; DN=800.18 mm; F=35 mm  [stored 0.114829 ft]; F1=15.75 mm  [stored 0.0516732 ft]; F2=116 mm; FL_T=43 mm; Fillet=104.27 mm; H1=1689 mm; H2=535 mm; L=660 mm; OD=1070 mm; OD1=1070 mm; PN=16 mm  [stored 0.0524934 ft]; Raised_dia=901 mm; Rib_Actual=744 mm; Rib_H=675.6 mm; Rib_H1=190 mm; Rib_H2=550 mm; Rib_H3=650 mm; Rib_H4=750 mm; Rib_L=522 mm; Rib_W=175.95 mm; Stem_D1=17.5 mm  [stored 0.0574147 ft]; Stem_D2=26.25 mm  [stored 0.086122 ft]; Stem_dim=43.75 mm; W=1488 mm; W-W1=580 mm; W1=908 mm; W_half=580 mm; bottom_rib=535 mm; stem_dim=38.67 mm; stem_dim1=56.88 mm; sweep=5 mm  [stored 0.0164042 ft]; sweep_start=450.5 mm; wedge_dim1=344.08 mm
- 54-0800-34-1102100: ACtuator_T=30.96 mm  [stored 0.101575 ft]; ADN=800 mm; Actuator_FLR=105 mm; Actuator_dim1=63 mm; Actuator_dim2=37.8 mm; Actuator_dim3=69.3 mm; Body_H=844.5 mm; Body_L=1102 mm; Body_T=392.5 mm; Body_W=312.8 mm; Body_rib_T=17.2 mm; Bonnet_FL_L=1160 mm; Bonnet_FL_T=81.7 mm; Bonnet_FL_W=391 mm; Bonnet_dim1=220.4 mm; Bonnet_dim2=109.48 mm; Bonnet_dim3=1452.54 mm; Bonnet_fillet=34.76 mm; Bore=400.1 mm; Bypass_D7=473.03 mm; Bypass_Location=172 mm; Bypass_Vale_D4=70.38 mm; Bypass_Vale_D5=98.53 mm; Bypass_Vale_T=56.3 mm; Bypass_sweep=473.03 mm; Cut_dis=40.85 mm; DN=800.19 mm; F=42 mm; F1=18.9 mm  [stored 0.0620079 ft]; F2=129 mm; FL_T=43 mm; Fillet=104.27 mm; H1=1689 mm; H2=535 mm; L=660 mm; OD=1070 mm; OD1=1070 mm; PN=16 mm  [stored 0.0524934 ft]; Raised_dia=901 mm; Rib_Actual=744 mm; Rib_H=675.6 mm; Rib_H1=190 mm; Rib_H2=550 mm; Rib_H3=650 mm; Rib_H4=750 mm; Rib_L=522 mm; Rib_W=175.95 mm; Stem_D1=21 mm  [stored 0.0688976 ft]; Stem_D2=31.5 mm  [stored 0.103346 ft]; Stem_dim=52.5 mm; W=1488 mm; W-W1=580 mm; W1=908 mm; W_half=580 mm; bottom_rib=535 mm; stem_dim=43 mm; stem_dim1=68.25 mm; sweep=5 mm  [stored 0.0164042 ft]; sweep_start=450.5 mm; wedge_dim1=344.08 mm
- 54-0900-33-0102100: ACtuator_T=27 mm  [stored 0.0885827 ft]; ADN=900 mm; Actuator_FLR=105 mm; Actuator_dim1=63 mm; Actuator_dim2=37.8 mm; Actuator_dim3=69.3 mm; Body_H=922 mm; Body_L=1102 mm; Body_T=392.5 mm; Body_W=312.8 mm; Body_rib_T=15 mm  [stored 0.0492126 ft]; Bonnet_FL_L=1160 mm; Bonnet_FL_T=71.25 mm; Bonnet_FL_W=391 mm; Bonnet_dim1=220.4 mm; Bonnet_dim2=109.48 mm; Bonnet_dim3=1585.84 mm; Bonnet_fillet=34.76 mm; Bore=450 mm; Bypass_D7=525.53 mm; Bypass_Location=208 mm; Bypass_Vale_D4=70.38 mm; Bypass_Vale_D5=98.53 mm; Bypass_Vale_T=56.3 mm; Bypass_sweep=525.53 mm; Cut_dis=35.63 mm; DN=900 mm; F=42 mm; F1=18.9 mm  [stored 0.0620079 ft]; F2=131 mm; FL_T=37.5 mm; Fillet=104.27 mm; H1=1844 mm; H2=596 mm; L=711 mm; OD=1115 mm; OD1=1192 mm; PN=10 mm  [stored 0.0328084 ft]; Raised_dia=1001 mm; Rib_Actual=801.5 mm; Rib_H=737.6 mm; Rib_H1=200 mm; Rib_H2=650 mm; Rib_H3=750 mm; Rib_H4=850 mm; Rib_L=522 mm; Rib_W=175.95 mm; Stem_D1=21 mm  [stored 0.0688976 ft]; Stem_D2=31.5 mm  [stored 0.103346 ft]; Stem_dim=52.5 mm; W=1603 mm; W-W1=655 mm; W1=948 mm; W_half=655 mm; bottom_rib=557.5 mm; stem_dim=43.67 mm; stem_dim1=68.25 mm; sweep=5 mm  [stored 0.0164042 ft]; sweep_start=500.5 mm; wedge_dim1=344.08 mm
- 54-0900-33-1101100: ACtuator_T=33.48 mm  [stored 0.109843 ft]; ADN=900 mm; Actuator_FLR=87.5 mm; Actuator_dim1=52.5 mm; Actuator_dim2=31.5 mm  [stored 0.103346 ft]; Actuator_dim3=57.75 mm; Body_H=922 mm; Body_L=1102 mm; Body_T=392.5 mm; Body_W=312.8 mm; Body_rib_T=18.6 mm  [stored 0.0610236 ft]; Bonnet_FL_L=1160 mm; Bonnet_FL_T=88.35 mm; Bonnet_FL_W=391 mm; Bonnet_dim1=220.4 mm; Bonnet_dim2=109.48 mm; Bonnet_dim3=1585.84 mm; Bonnet_fillet=34.76 mm; Bore=450.05 mm; Bypass_D7=525.53 mm; Bypass_Location=208 mm; Bypass_Vale_D4=70.38 mm; Bypass_Vale_D5=98.53 mm; Bypass_Vale_T=56.3 mm; Bypass_sweep=525.53 mm; Cut_dis=44.18 mm; DN=900.1 mm; F=35 mm  [stored 0.114829 ft]; F1=15.75 mm  [stored 0.0516732 ft]; F2=118 mm; FL_T=46.5 mm; Fillet=104.27 mm; H1=1844 mm; H2=596 mm; L=711 mm; OD=1070 mm; OD1=1192 mm; PN=16 mm  [stored 0.0524934 ft]; Raised_dia=1001 mm; Rib_Actual=801.5 mm; Rib_H=737.6 mm; Rib_H1=200 mm; Rib_H2=650 mm; Rib_H3=750 mm; Rib_H4=850 mm; Rib_L=522 mm; Rib_W=175.95 mm; Stem_D1=17.5 mm  [stored 0.0574147 ft]; Stem_D2=26.25 mm  [stored 0.086122 ft]; Stem_dim=43.75 mm; W=1603 mm; W-W1=655 mm; W1=948 mm; W_half=655 mm; bottom_rib=535 mm; stem_dim=39.33 mm; stem_dim1=56.88 mm; sweep=5 mm  [stored 0.0164042 ft]; sweep_start=500.5 mm; wedge_dim1=344.08 mm
- 54-0900-33-1102100: ACtuator_T=33.48 mm  [stored 0.109843 ft]; ADN=900 mm; Actuator_FLR=105 mm; Actuator_dim1=63 mm; Actuator_dim2=37.8 mm; Actuator_dim3=69.3 mm; Body_H=922 mm; Body_L=1102 mm; Body_T=392.5 mm; Body_W=312.8 mm; Body_rib_T=18.6 mm  [stored 0.0610236 ft]; Bonnet_FL_L=1160 mm; Bonnet_FL_T=88.35 mm; Bonnet_FL_W=391 mm; Bonnet_dim1=220.4 mm; Bonnet_dim2=109.48 mm; Bonnet_dim3=1585.84 mm; Bonnet_fillet=34.76 mm; Bore=450.06 mm; Bypass_D7=525.53 mm; Bypass_Location=208 mm; Bypass_Vale_D4=70.38 mm; Bypass_Vale_D5=98.53 mm; Bypass_Vale_T=56.3 mm; Bypass_sweep=525.53 mm; Cut_dis=44.18 mm; DN=900.11 mm; F=42 mm; F1=18.9 mm  [stored 0.0620079 ft]; F2=131 mm; FL_T=46.5 mm; Fillet=104.27 mm; H1=1844 mm; H2=596 mm; L=711 mm; OD=1070 mm; OD1=1192 mm; PN=16 mm  [stored 0.0524934 ft]; Raised_dia=1001 mm; Rib_Actual=801.5 mm; Rib_H=737.6 mm; Rib_H1=200 mm; Rib_H2=650 mm; Rib_H3=750 mm; Rib_H4=850 mm; Rib_L=522 mm; Rib_W=175.95 mm; Stem_D1=21 mm  [stored 0.0688976 ft]; Stem_D2=31.5 mm  [stored 0.103346 ft]; Stem_dim=52.5 mm; W=1603 mm; W-W1=655 mm; W1=948 mm; W_half=655 mm; bottom_rib=535 mm; stem_dim=43.67 mm; stem_dim1=68.25 mm; sweep=5 mm  [stored 0.0164042 ft]; sweep_start=500.5 mm; wedge_dim1=344.08 mm
- 54-0900-33-1103100: ACtuator_T=33.48 mm  [stored 0.109843 ft]; ADN=900 mm; Actuator_FLR=150 mm; Actuator_dim1=90 mm; Actuator_dim2=54 mm; Actuator_dim3=99 mm; Body_H=922 mm; Body_L=1102 mm; Body_T=392.5 mm; Body_W=312.8 mm; Body_rib_T=18.6 mm  [stored 0.0610236 ft]; Bonnet_FL_L=1160 mm; Bonnet_FL_T=88.35 mm; Bonnet_FL_W=391 mm; Bonnet_dim1=220.4 mm; Bonnet_dim2=109.48 mm; Bonnet_dim3=1585.84 mm; Bonnet_fillet=34.76 mm; Bore=450.06 mm; Bypass_D7=525.53 mm; Bypass_Location=208 mm; Bypass_Vale_D4=70.38 mm; Bypass_Vale_D5=98.53 mm; Bypass_Vale_T=56.3 mm; Bypass_sweep=525.53 mm; Cut_dis=44.18 mm; DN=900.12 mm; F=60 mm; F1=27 mm  [stored 0.0885827 ft]; F2=171 mm; FL_T=46.5 mm; Fillet=104.27 mm; H1=1844 mm; H2=596 mm; L=711 mm; OD=1070 mm; OD1=1192 mm; PN=16 mm  [stored 0.0524934 ft]; Raised_dia=1001 mm; Rib_Actual=801.5 mm; Rib_H=737.6 mm; Rib_H1=200 mm; Rib_H2=650 mm; Rib_H3=750 mm; Rib_H4=850 mm; Rib_L=522 mm; Rib_W=175.95 mm; Stem_D1=30 mm  [stored 0.0984252 ft]; Stem_D2=45 mm; Stem_dim=75 mm; W=1603 mm; W-W1=655 mm; W1=948 mm; W_half=655 mm; bottom_rib=535 mm; stem_dim=57 mm; stem_dim1=97.5 mm; sweep=5 mm  [stored 0.0164042 ft]; sweep_start=500.5 mm; wedge_dim1=344.08 mm
- 54-0900-33-1104100: ACtuator_T=33.48 mm  [stored 0.109843 ft]; ADN=900 mm; Actuator_FLR=175 mm; Actuator_dim1=105 mm; Actuator_dim2=63 mm; Actuator_dim3=115.5 mm; Body_H=922 mm; Body_L=1238.8 mm; Body_T=442.5 mm; Body_W=341.6 mm; Body_rib_T=18.6 mm  [stored 0.0610236 ft]; Bonnet_FL_L=1304 mm; Bonnet_FL_T=88.35 mm; Bonnet_FL_W=427 mm; Bonnet_dim1=247.76 mm; Bonnet_dim2=119.56 mm; Bonnet_dim3=1585.84 mm; Bonnet_fillet=37.96 mm; Bore=450.07 mm; Bypass_D7=525.53 mm; Bypass_Location=208 mm; Bypass_Vale_D4=76.86 mm; Bypass_Vale_D5=107.6 mm; Bypass_Vale_T=61.49 mm; Bypass_sweep=525.53 mm; Cut_dis=44.18 mm; DN=900.13 mm; F=70 mm; F1=31.5 mm  [stored 0.103346 ft]; F2=201 mm; FL_T=46.5 mm; Fillet=113.87 mm; H1=1844 mm; H2=596 mm; L=711 mm; OD=1192 mm; OD1=1192 mm; PN=16 mm  [stored 0.0524934 ft]; Raised_dia=1001 mm; Rib_Actual=801.5 mm; Rib_H=737.6 mm; Rib_H1=200 mm; Rib_H2=650 mm; Rib_H3=750 mm; Rib_H4=850 mm; Rib_L=586.8 mm; Rib_W=192.15 mm; Stem_D1=35 mm  [stored 0.114829 ft]; Stem_D2=52.5 mm; Stem_dim=87.5 mm; W=1603 mm; W-W1=655 mm; W1=948 mm; W_half=655 mm; bottom_rib=596 mm; stem_dim=67 mm; stem_dim1=113.75 mm; sweep=5 mm  [stored 0.0164042 ft]; sweep_start=500.5 mm; wedge_dim1=375.76 mm
- 54-0900-34-0102100: ACtuator_T=27 mm  [stored 0.0885827 ft]; ADN=900 mm; Actuator_FLR=105 mm; Actuator_dim1=63 mm; Actuator_dim2=37.8 mm; Actuator_dim3=69.3 mm; Body_H=922 mm; Body_L=1238.8 mm; Body_T=442.5 mm; Body_W=341.6 mm; Body_rib_T=15 mm  [stored 0.0492126 ft]; Bonnet_FL_L=1304 mm; Bonnet_FL_T=71.25 mm; Bonnet_FL_W=427 mm; Bonnet_dim1=247.76 mm; Bonnet_dim2=119.56 mm; Bonnet_dim3=1585.84 mm; Bonnet_fillet=37.96 mm; Bore=450.07 mm; Bypass_D7=525.53 mm; Bypass_Location=208 mm; Bypass_Vale_D4=76.86 mm; Bypass_Vale_D5=107.6 mm; Bypass_Vale_T=61.49 mm; Bypass_sweep=525.53 mm; Cut_dis=35.63 mm; DN=900.14 mm; F=42 mm; F1=18.9 mm  [stored 0.0620079 ft]; F2=131 mm; FL_T=37.5 mm; Fillet=113.87 mm; H1=1844 mm; H2=596 mm; L=711 mm; OD=1115 mm; OD1=1192 mm; PN=10 mm  [stored 0.0328084 ft]; Raised_dia=1001 mm; Rib_Actual=801.5 mm; Rib_H=737.6 mm; Rib_H1=200 mm; Rib_H2=650 mm; Rib_H3=750 mm; Rib_H4=850 mm; Rib_L=586.8 mm; Rib_W=192.15 mm; Stem_D1=21 mm  [stored 0.0688976 ft]; Stem_D2=31.5 mm  [stored 0.103346 ft]; Stem_dim=52.5 mm; W=1603 mm; W-W1=655 mm; W1=948 mm; W_half=655 mm; bottom_rib=557.5 mm; stem_dim=43.67 mm; stem_dim1=68.25 mm; sweep=5 mm  [stored 0.0164042 ft]; sweep_start=500.5 mm; wedge_dim1=375.76 mm
- 54-0900-34-0104100: ACtuator_T=27 mm  [stored 0.0885827 ft]; ADN=900 mm; Actuator_FLR=175 mm; Actuator_dim1=105 mm; Actuator_dim2=63 mm; Actuator_dim3=115.5 mm; Body_H=922 mm; Body_L=1238.8 mm; Body_T=442.5 mm; Body_W=341.6 mm; Body_rib_T=15 mm  [stored 0.0492126 ft]; Bonnet_FL_L=1304 mm; Bonnet_FL_T=71.25 mm; Bonnet_FL_W=427 mm; Bonnet_dim1=247.76 mm; Bonnet_dim2=119.56 mm; Bonnet_dim3=1585.84 mm; Bonnet_fillet=37.96 mm; Bore=450.08 mm; Bypass_D7=525.53 mm; Bypass_Location=208 mm; Bypass_Vale_D4=76.86 mm; Bypass_Vale_D5=107.6 mm; Bypass_Vale_T=61.49 mm; Bypass_sweep=525.53 mm; Cut_dis=35.63 mm; DN=900.15 mm; F=70 mm; F1=31.5 mm  [stored 0.103346 ft]; F2=201 mm; FL_T=37.5 mm; Fillet=113.87 mm; H1=1844 mm; H2=596 mm; L=711 mm; OD=1115 mm; OD1=1192 mm; PN=10 mm  [stored 0.0328084 ft]; Raised_dia=1001 mm; Rib_Actual=801.5 mm; Rib_H=737.6 mm; Rib_H1=200 mm; Rib_H2=650 mm; Rib_H3=750 mm; Rib_H4=850 mm; Rib_L=586.8 mm; Rib_W=192.15 mm; Stem_D1=35 mm  [stored 0.114829 ft]; Stem_D2=52.5 mm; Stem_dim=87.5 mm; W=1603 mm; W-W1=655 mm; W1=948 mm; W_half=655 mm; bottom_rib=557.5 mm; stem_dim=67 mm; stem_dim1=113.75 mm; sweep=5 mm  [stored 0.0164042 ft]; sweep_start=500.5 mm; wedge_dim1=375.76 mm
- 54-0900-34-1101100: ACtuator_T=33.48 mm  [stored 0.109843 ft]; ADN=900 mm; Actuator_FLR=87.5 mm; Actuator_dim1=52.5 mm; Actuator_dim2=31.5 mm  [stored 0.103346 ft]; Actuator_dim3=57.75 mm; Body_H=922 mm; Body_L=1238.8 mm; Body_T=442.5 mm; Body_W=341.6 mm; Body_rib_T=18.6 mm  [stored 0.0610236 ft]; Bonnet_FL_L=1304 mm; Bonnet_FL_T=88.35 mm; Bonnet_FL_W=427 mm; Bonnet_dim1=247.76 mm; Bonnet_dim2=119.56 mm; Bonnet_dim3=1585.84 mm; Bonnet_fillet=37.96 mm; Bore=450.08 mm; Bypass_D7=525.53 mm; Bypass_Location=208 mm; Bypass_Vale_D4=76.86 mm; Bypass_Vale_D5=107.6 mm; Bypass_Vale_T=61.49 mm; Bypass_sweep=525.53 mm; Cut_dis=44.18 mm; DN=900.16 mm; F=35 mm  [stored 0.114829 ft]; F1=15.75 mm  [stored 0.0516732 ft]; F2=118 mm; FL_T=46.5 mm; Fillet=113.87 mm; H1=1844 mm; H2=596 mm; L=711 mm; OD=1192 mm; OD1=1192 mm; PN=16 mm  [stored 0.0524934 ft]; Raised_dia=1001 mm; Rib_Actual=801.5 mm; Rib_H=737.6 mm; Rib_H1=200 mm; Rib_H2=650 mm; Rib_H3=750 mm; Rib_H4=850 mm; Rib_L=586.8 mm; Rib_W=192.15 mm; Stem_D1=17.5 mm  [stored 0.0574147 ft]; Stem_D2=26.25 mm  [stored 0.086122 ft]; Stem_dim=43.75 mm; W=1603 mm; W-W1=655 mm; W1=948 mm; W_half=655 mm; bottom_rib=596 mm; stem_dim=39.33 mm; stem_dim1=56.88 mm; sweep=5 mm  [stored 0.0164042 ft]; sweep_start=500.5 mm; wedge_dim1=375.76 mm
- 54-0900-34-1102100: ACtuator_T=33.48 mm  [stored 0.109843 ft]; ADN=900 mm; Actuator_FLR=105 mm; Actuator_dim1=63 mm; Actuator_dim2=37.8 mm; Actuator_dim3=69.3 mm; Body_H=922 mm; Body_L=1238.8 mm; Body_T=442.5 mm; Body_W=341.6 mm; Body_rib_T=18.6 mm  [stored 0.0610236 ft]; Bonnet_FL_L=1304 mm; Bonnet_FL_T=88.35 mm; Bonnet_FL_W=427 mm; Bonnet_dim1=247.76 mm; Bonnet_dim2=119.56 mm; Bonnet_dim3=1585.84 mm; Bonnet_fillet=37.96 mm; Bore=450.09 mm; Bypass_D7=525.53 mm; Bypass_Location=208 mm; Bypass_Vale_D4=76.86 mm; Bypass_Vale_D5=107.6 mm; Bypass_Vale_T=61.49 mm; Bypass_sweep=525.53 mm; Cut_dis=44.18 mm; DN=900.17 mm; F=42 mm; F1=18.9 mm  [stored 0.0620079 ft]; F2=131 mm; FL_T=46.5 mm; Fillet=113.87 mm; H1=1844 mm; H2=596 mm; L=711 mm; OD=1192 mm; OD1=1192 mm; PN=16 mm  [stored 0.0524934 ft]; Raised_dia=1001 mm; Rib_Actual=801.5 mm; Rib_H=737.6 mm; Rib_H1=200 mm; Rib_H2=650 mm; Rib_H3=750 mm; Rib_H4=850 mm; Rib_L=586.8 mm; Rib_W=192.15 mm; Stem_D1=21 mm  [stored 0.0688976 ft]; Stem_D2=31.5 mm  [stored 0.103346 ft]; Stem_dim=52.5 mm; W=1603 mm; W-W1=655 mm; W1=948 mm; W_half=655 mm; bottom_rib=596 mm; stem_dim=43.67 mm; stem_dim1=68.25 mm; sweep=5 mm  [stored 0.0164042 ft]; sweep_start=500.5 mm; wedge_dim1=375.76 mm
- 54-0900-34-1103100: ACtuator_T=33.48 mm  [stored 0.109843 ft]; ADN=900 mm; Actuator_FLR=150 mm; Actuator_dim1=90 mm; Actuator_dim2=54 mm; Actuator_dim3=99 mm; Body_H=922 mm; Body_L=1238.8 mm; Body_T=442.5 mm; Body_W=341.6 mm; Body_rib_T=18.6 mm  [stored 0.0610236 ft]; Bonnet_FL_L=1304 mm; Bonnet_FL_T=88.35 mm; Bonnet_FL_W=427 mm; Bonnet_dim1=247.76 mm; Bonnet_dim2=119.56 mm; Bonnet_dim3=1585.84 mm; Bonnet_fillet=37.96 mm; Bore=450.09 mm; Bypass_D7=525.53 mm; Bypass_Location=208 mm; Bypass_Vale_D4=76.86 mm; Bypass_Vale_D5=107.6 mm; Bypass_Vale_T=61.49 mm; Bypass_sweep=525.53 mm; Cut_dis=44.18 mm; DN=900.18 mm; F=60 mm; F1=27 mm  [stored 0.0885827 ft]; F2=171 mm; FL_T=46.5 mm; Fillet=113.87 mm; H1=1844 mm; H2=596 mm; L=711 mm; OD=1192 mm; OD1=1192 mm; PN=16 mm  [stored 0.0524934 ft]; Raised_dia=1001 mm; Rib_Actual=801.5 mm; Rib_H=737.6 mm; Rib_H1=200 mm; Rib_H2=650 mm; Rib_H3=750 mm; Rib_H4=850 mm; Rib_L=586.8 mm; Rib_W=192.15 mm; Stem_D1=30 mm  [stored 0.0984252 ft]; Stem_D2=45 mm; Stem_dim=75 mm; W=1603 mm; W-W1=655 mm; W1=948 mm; W_half=655 mm; bottom_rib=596 mm; stem_dim=57 mm; stem_dim1=97.5 mm; sweep=5 mm  [stored 0.0164042 ft]; sweep_start=500.5 mm; wedge_dim1=375.76 mm
- 54-1000-33-0102100: ACtuator_T=28.8 mm  [stored 0.0944882 ft]; ADN=1000 mm; Actuator_FLR=105 mm; Actuator_dim1=63 mm; Actuator_dim2=37.8 mm; Actuator_dim3=69.3 mm; Body_H=1003.5 mm; Body_L=1238.8 mm; Body_T=442.5 mm; Body_W=341.6 mm; Body_rib_T=16 mm  [stored 0.0524934 ft]; Bonnet_FL_L=1304 mm; Bonnet_FL_T=76 mm; Bonnet_FL_W=427 mm; Bonnet_dim1=247.76 mm; Bonnet_dim2=119.56 mm; Bonnet_dim3=1726.02 mm; Bonnet_fillet=37.96 mm; Bore=500 mm; Bypass_D7=583.8 mm; Bypass_Location=208 mm; Bypass_Vale_D4=76.86 mm; Bypass_Vale_D5=107.6 mm; Bypass_Vale_T=61.49 mm; Bypass_sweep=583.8 mm; Cut_dis=38 mm; DN=1000 mm; F=42 mm; F1=18.9 mm  [stored 0.0620079 ft]; F2=136 mm; FL_T=40 mm; Fillet=113.87 mm; H1=2007 mm; H2=648 mm; L=813 mm; OD=1230 mm; OD1=1296 mm; PN=10 mm  [stored 0.0328084 ft]; Raised_dia=1112 mm; Rib_Actual=853.5 mm; Rib_H=802.8 mm; Rib_H1=235 mm; Rib_H2=680 mm; Rib_H3=780 mm; Rib_H4=880 mm; Rib_L=586.8 mm; Rib_W=192.15 mm; Stem_D1=21 mm  [stored 0.0688976 ft]; Stem_D2=31.5 mm  [stored 0.103346 ft]; Stem_dim=52.5 mm; W=1707 mm; W-W1=702 mm; W1=1005 mm; W_half=702 mm; bottom_rib=615 mm; stem_dim=45.33 mm; stem_dim1=68.25 mm; sweep=5 mm  [stored 0.0164042 ft]; sweep_start=556 mm; wedge_dim1=375.76 mm
- 54-1000-33-0103100: ACtuator_T=28.8 mm  [stored 0.0944882 ft]; ADN=1000 mm; Actuator_FLR=150 mm; Actuator_dim1=90 mm; Actuator_dim2=54 mm; Actuator_dim3=99 mm; Body_H=1003.5 mm; Body_L=1238.8 mm; Body_T=442.5 mm; Body_W=341.6 mm; Body_rib_T=16 mm  [stored 0.0524934 ft]; Bonnet_FL_L=1304 mm; Bonnet_FL_T=76 mm; Bonnet_FL_W=427 mm; Bonnet_dim1=247.76 mm; Bonnet_dim2=119.56 mm; Bonnet_dim3=1726.02 mm; Bonnet_fillet=37.96 mm; Bore=500.05 mm; Bypass_D7=583.8 mm; Bypass_Location=208 mm; Bypass_Vale_D4=76.86 mm; Bypass_Vale_D5=107.6 mm; Bypass_Vale_T=61.49 mm; Bypass_sweep=583.8 mm; Cut_dis=38 mm; DN=1000.1 mm; F=60 mm; F1=27 mm  [stored 0.0885827 ft]; F2=176 mm; FL_T=40 mm; Fillet=113.87 mm; H1=2007 mm; H2=648 mm; L=813 mm; OD=1230 mm; OD1=1296 mm; PN=10 mm  [stored 0.0328084 ft]; Raised_dia=1112 mm; Rib_Actual=853.5 mm; Rib_H=802.8 mm; Rib_H1=235 mm; Rib_H2=680 mm; Rib_H3=780 mm; Rib_H4=880 mm; Rib_L=586.8 mm; Rib_W=192.15 mm; Stem_D1=30 mm  [stored 0.0984252 ft]; Stem_D2=45 mm; Stem_dim=75 mm; W=1707 mm; W-W1=702 mm; W1=1005 mm; W_half=702 mm; bottom_rib=615 mm; stem_dim=58.67 mm; stem_dim1=97.5 mm; sweep=5 mm  [stored 0.0164042 ft]; sweep_start=556 mm; wedge_dim1=375.76 mm
- 54-1000-33-0104100: ACtuator_T=28.8 mm  [stored 0.0944882 ft]; ADN=1000 mm; Actuator_FLR=175 mm; Actuator_dim1=105 mm; Actuator_dim2=63 mm; Actuator_dim3=115.5 mm; Body_H=1003.5 mm; Body_L=1238.8 mm; Body_T=442.5 mm; Body_W=341.6 mm; Body_rib_T=16 mm  [stored 0.0524934 ft]; Bonnet_FL_L=1304 mm; Bonnet_FL_T=76 mm; Bonnet_FL_W=427 mm; Bonnet_dim1=247.76 mm; Bonnet_dim2=119.56 mm; Bonnet_dim3=1726.02 mm; Bonnet_fillet=37.96 mm; Bore=500.06 mm; Bypass_D7=583.8 mm; Bypass_Location=208 mm; Bypass_Vale_D4=76.86 mm; Bypass_Vale_D5=107.6 mm; Bypass_Vale_T=61.49 mm; Bypass_sweep=583.8 mm; Cut_dis=38 mm; DN=1000.11 mm; F=70 mm; F1=31.5 mm  [stored 0.103346 ft]; F2=206 mm; FL_T=40 mm; Fillet=113.87 mm; H1=2007 mm; H2=648 mm; L=813 mm; OD=1230 mm; OD1=1296 mm; PN=10 mm  [stored 0.0328084 ft]; Raised_dia=1112 mm; Rib_Actual=853.5 mm; Rib_H=802.8 mm; Rib_H1=235 mm; Rib_H2=680 mm; Rib_H3=780 mm; Rib_H4=880 mm; Rib_L=586.8 mm; Rib_W=192.15 mm; Stem_D1=35 mm  [stored 0.114829 ft]; Stem_D2=52.5 mm; Stem_dim=87.5 mm; W=1707 mm; W-W1=702 mm; W1=1005 mm; W_half=702 mm; bottom_rib=615 mm; stem_dim=68.67 mm; stem_dim1=113.75 mm; sweep=5 mm  [stored 0.0164042 ft]; sweep_start=556 mm; wedge_dim1=375.76 mm
- 54-1000-33-1102100: ACtuator_T=36 mm  [stored 0.11811 ft]; ADN=1000 mm; Actuator_FLR=105 mm; Actuator_dim1=63 mm; Actuator_dim2=37.8 mm; Actuator_dim3=69.3 mm; Body_H=1003.5 mm; Body_L=1324.3 mm; Body_T=492.5 mm; Body_W=424.8 mm; Body_rib_T=20 mm  [stored 0.0656168 ft]; Bonnet_FL_L=1394 mm; Bonnet_FL_T=95 mm; Bonnet_FL_W=531 mm; Bonnet_dim1=264.86 mm; Bonnet_dim2=148.68 mm; Bonnet_dim3=1726.02 mm; Bonnet_fillet=47.2 mm; Bore=500.06 mm; Bypass_D7=583.8 mm; Bypass_Location=208 mm; Bypass_Vale_D4=95.58 mm; Bypass_Vale_D5=133.81 mm; Bypass_Vale_T=76.46 mm; Bypass_sweep=583.8 mm; Cut_dis=47.5 mm; DN=1000.12 mm; F=42 mm; F1=18.9 mm  [stored 0.0620079 ft]; F2=136 mm; FL_T=50 mm; Fillet=141.6 mm; H1=2007 mm; H2=648 mm; L=813 mm; OD=1296 mm; OD1=1296 mm; PN=16 mm  [stored 0.0524934 ft]; Raised_dia=1112 mm; Rib_Actual=853.5 mm; Rib_H=802.8 mm; Rib_H1=235 mm; Rib_H2=680 mm; Rib_H3=780 mm; Rib_H4=880 mm; Rib_L=627.3 mm; Rib_W=238.95 mm; Stem_D1=21 mm  [stored 0.0688976 ft]; Stem_D2=31.5 mm  [stored 0.103346 ft]; Stem_dim=52.5 mm; W=1707 mm; W-W1=702 mm; W1=1005 mm; W_half=702 mm; bottom_rib=648 mm; stem_dim=45.33 mm; stem_dim1=68.25 mm; sweep=5 mm  [stored 0.0164042 ft]; sweep_start=556 mm; wedge_dim1=467.28 mm
- 54-1000-33-1103100: ACtuator_T=36 mm  [stored 0.11811 ft]; ADN=1000 mm; Actuator_FLR=150 mm; Actuator_dim1=90 mm; Actuator_dim2=54 mm; Actuator_dim3=99 mm; Body_H=1003.5 mm; Body_L=1324.3 mm; Body_T=492.5 mm; Body_W=424.8 mm; Body_rib_T=20 mm  [stored 0.0656168 ft]; Bonnet_FL_L=1394 mm; Bonnet_FL_T=95 mm; Bonnet_FL_W=531 mm; Bonnet_dim1=264.86 mm; Bonnet_dim2=148.68 mm; Bonnet_dim3=1726.02 mm; Bonnet_fillet=47.2 mm; Bore=500.07 mm; Bypass_D7=583.8 mm; Bypass_Location=208 mm; Bypass_Vale_D4=95.58 mm; Bypass_Vale_D5=133.81 mm; Bypass_Vale_T=76.46 mm; Bypass_sweep=583.8 mm; Cut_dis=47.5 mm; DN=1000.13 mm; F=60 mm; F1=27 mm  [stored 0.0885827 ft]; F2=176 mm; FL_T=50 mm; Fillet=141.6 mm; H1=2007 mm; H2=648 mm; L=813 mm; OD=1296 mm; OD1=1296 mm; PN=16 mm  [stored 0.0524934 ft]; Raised_dia=1112 mm; Rib_Actual=853.5 mm; Rib_H=802.8 mm; Rib_H1=235 mm; Rib_H2=680 mm; Rib_H3=780 mm; Rib_H4=880 mm; Rib_L=627.3 mm; Rib_W=238.95 mm; Stem_D1=30 mm  [stored 0.0984252 ft]; Stem_D2=45 mm; Stem_dim=75 mm; W=1707 mm; W-W1=702 mm; W1=1005 mm; W_half=702 mm; bottom_rib=648 mm; stem_dim=58.67 mm; stem_dim1=97.5 mm; sweep=5 mm  [stored 0.0164042 ft]; sweep_start=556 mm; wedge_dim1=467.28 mm
- 54-1000-33-1104100: ACtuator_T=36 mm  [stored 0.11811 ft]; ADN=1000 mm; Actuator_FLR=175 mm; Actuator_dim1=105 mm; Actuator_dim2=63 mm; Actuator_dim3=115.5 mm; Body_H=1003.5 mm; Body_L=1324.3 mm; Body_T=492.5 mm; Body_W=424.8 mm; Body_rib_T=20 mm  [stored 0.0656168 ft]; Bonnet_FL_L=1394 mm; Bonnet_FL_T=95 mm; Bonnet_FL_W=531 mm; Bonnet_dim1=264.86 mm; Bonnet_dim2=148.68 mm; Bonnet_dim3=1726.02 mm; Bonnet_fillet=47.2 mm; Bore=500.07 mm; Bypass_D7=583.8 mm; Bypass_Location=208 mm; Bypass_Vale_D4=95.58 mm; Bypass_Vale_D5=133.81 mm; Bypass_Vale_T=76.46 mm; Bypass_sweep=583.8 mm; Cut_dis=47.5 mm; DN=1000.14 mm; F=70 mm; F1=31.5 mm  [stored 0.103346 ft]; F2=206 mm; FL_T=50 mm; Fillet=141.6 mm; H1=2007 mm; H2=648 mm; L=813 mm; OD=1296 mm; OD1=1296 mm; PN=16 mm  [stored 0.0524934 ft]; Raised_dia=1112 mm; Rib_Actual=853.5 mm; Rib_H=802.8 mm; Rib_H1=235 mm; Rib_H2=680 mm; Rib_H3=780 mm; Rib_H4=880 mm; Rib_L=627.3 mm; Rib_W=238.95 mm; Stem_D1=35 mm  [stored 0.114829 ft]; Stem_D2=52.5 mm; Stem_dim=87.5 mm; W=1707 mm; W-W1=702 mm; W1=1005 mm; W_half=702 mm; bottom_rib=648 mm; stem_dim=68.67 mm; stem_dim1=113.75 mm; sweep=5 mm  [stored 0.0164042 ft]; sweep_start=556 mm; wedge_dim1=467.28 mm
- 54-1000-34-0102100: ACtuator_T=28.8 mm  [stored 0.0944882 ft]; ADN=1000 mm; Actuator_FLR=105 mm; Actuator_dim1=63 mm; Actuator_dim2=37.8 mm; Actuator_dim3=69.3 mm; Body_H=1003.5 mm; Body_L=1324.3 mm; Body_T=492.5 mm; Body_W=424.8 mm; Body_rib_T=16 mm  [stored 0.0524934 ft]; Bonnet_FL_L=1394 mm; Bonnet_FL_T=76 mm; Bonnet_FL_W=531 mm; Bonnet_dim1=264.86 mm; Bonnet_dim2=148.68 mm; Bonnet_dim3=1726.02 mm; Bonnet_fillet=47.2 mm; Bore=500.08 mm; Bypass_D7=583.8 mm; Bypass_Location=208 mm; Bypass_Vale_D4=95.58 mm; Bypass_Vale_D5=133.81 mm; Bypass_Vale_T=76.46 mm; Bypass_sweep=583.8 mm; Cut_dis=38 mm; DN=1000.15 mm; F=42 mm; F1=18.9 mm  [stored 0.0620079 ft]; F2=136 mm; FL_T=40 mm; Fillet=141.6 mm; H1=2007 mm; H2=648 mm; L=813 mm; OD=1230 mm; OD1=1296 mm; PN=10 mm  [stored 0.0328084 ft]; Raised_dia=1112 mm; Rib_Actual=853.5 mm; Rib_H=802.8 mm; Rib_H1=235 mm; Rib_H2=680 mm; Rib_H3=780 mm; Rib_H4=880 mm; Rib_L=627.3 mm; Rib_W=238.95 mm; Stem_D1=21 mm  [stored 0.0688976 ft]; Stem_D2=31.5 mm  [stored 0.103346 ft]; Stem_dim=52.5 mm; W=1707 mm; W-W1=702 mm; W1=1005 mm; W_half=702 mm; bottom_rib=615 mm; stem_dim=45.33 mm; stem_dim1=68.25 mm; sweep=5 mm  [stored 0.0164042 ft]; sweep_start=556 mm; wedge_dim1=467.28 mm
- 54-1000-34-1102100: ACtuator_T=28.8 mm  [stored 0.0944882 ft]; ADN=1000 mm; Actuator_FLR=105 mm; Actuator_dim1=63 mm; Actuator_dim2=37.8 mm; Actuator_dim3=69.3 mm; Body_H=1003.5 mm; Body_L=1324.3 mm; Body_T=492.5 mm; Body_W=424.8 mm; Body_rib_T=16 mm  [stored 0.0524934 ft]; Bonnet_FL_L=1394 mm; Bonnet_FL_T=76 mm; Bonnet_FL_W=531 mm; Bonnet_dim1=264.86 mm; Bonnet_dim2=148.68 mm; Bonnet_dim3=1726.02 mm; Bonnet_fillet=47.2 mm; Bore=500.08 mm; Bypass_D7=583.8 mm; Bypass_Location=208 mm; Bypass_Vale_D4=95.58 mm; Bypass_Vale_D5=133.81 mm; Bypass_Vale_T=76.46 mm; Bypass_sweep=583.8 mm; Cut_dis=38 mm; DN=1000.15 mm; F=42 mm; F1=18.9 mm  [stored 0.0620079 ft]; F2=136 mm; FL_T=40 mm; Fillet=141.6 mm; H1=2007 mm; H2=648 mm; L=813 mm; OD=1230 mm; OD1=1296 mm; PN=10 mm  [stored 0.0328084 ft]; Raised_dia=1112 mm; Rib_Actual=853.5 mm; Rib_H=802.8 mm; Rib_H1=235 mm; Rib_H2=680 mm; Rib_H3=780 mm; Rib_H4=880 mm; Rib_L=627.3 mm; Rib_W=238.95 mm; Stem_D1=21 mm  [stored 0.0688976 ft]; Stem_D2=31.5 mm  [stored 0.103346 ft]; Stem_dim=52.5 mm; W=1707 mm; W-W1=702 mm; W1=1005 mm; W_half=702 mm; bottom_rib=615 mm; stem_dim=45.33 mm; stem_dim1=68.25 mm; sweep=5 mm  [stored 0.0164042 ft]; sweep_start=556 mm; wedge_dim1=467.28 mm
- 54-1000-34-1103100: ACtuator_T=36 mm  [stored 0.11811 ft]; ADN=1000 mm; Actuator_FLR=105 mm; Actuator_dim1=63 mm; Actuator_dim2=37.8 mm; Actuator_dim3=69.3 mm; Body_H=1003.5 mm; Body_L=1324.3 mm; Body_T=492.5 mm; Body_W=424.8 mm; Body_rib_T=20 mm  [stored 0.0656168 ft]; Bonnet_FL_L=1394 mm; Bonnet_FL_T=95 mm; Bonnet_FL_W=531 mm; Bonnet_dim1=264.86 mm; Bonnet_dim2=148.68 mm; Bonnet_dim3=1726.02 mm; Bonnet_fillet=47.2 mm; Bore=500.08 mm; Bypass_D7=583.8 mm; Bypass_Location=208 mm; Bypass_Vale_D4=95.58 mm; Bypass_Vale_D5=133.81 mm; Bypass_Vale_T=76.46 mm; Bypass_sweep=583.8 mm; Cut_dis=47.5 mm; DN=1000.16 mm; F=42 mm; F1=18.9 mm  [stored 0.0620079 ft]; F2=136 mm; FL_T=50 mm; Fillet=141.6 mm; H1=2007 mm; H2=648 mm; L=813 mm; OD=1296 mm; OD1=1296 mm; PN=16 mm  [stored 0.0524934 ft]; Raised_dia=1112 mm; Rib_Actual=853.5 mm; Rib_H=802.8 mm; Rib_H1=235 mm; Rib_H2=680 mm; Rib_H3=780 mm; Rib_H4=880 mm; Rib_L=627.3 mm; Rib_W=238.95 mm; Stem_D1=21 mm  [stored 0.0688976 ft]; Stem_D2=31.5 mm  [stored 0.103346 ft]; Stem_dim=52.5 mm; W=1707 mm; W-W1=702 mm; W1=1005 mm; W_half=702 mm; bottom_rib=648 mm; stem_dim=45.33 mm; stem_dim1=68.25 mm; sweep=5 mm  [stored 0.0164042 ft]; sweep_start=556 mm; wedge_dim1=467.28 mm

note: [stored X ft] marks values corroborated as IEEE doubles in the binary element streams (Revit-internal decimal feet)

## geometry (parser evidence)
native form markers: Sweep x5
no freeform markers — native parametric forms only
